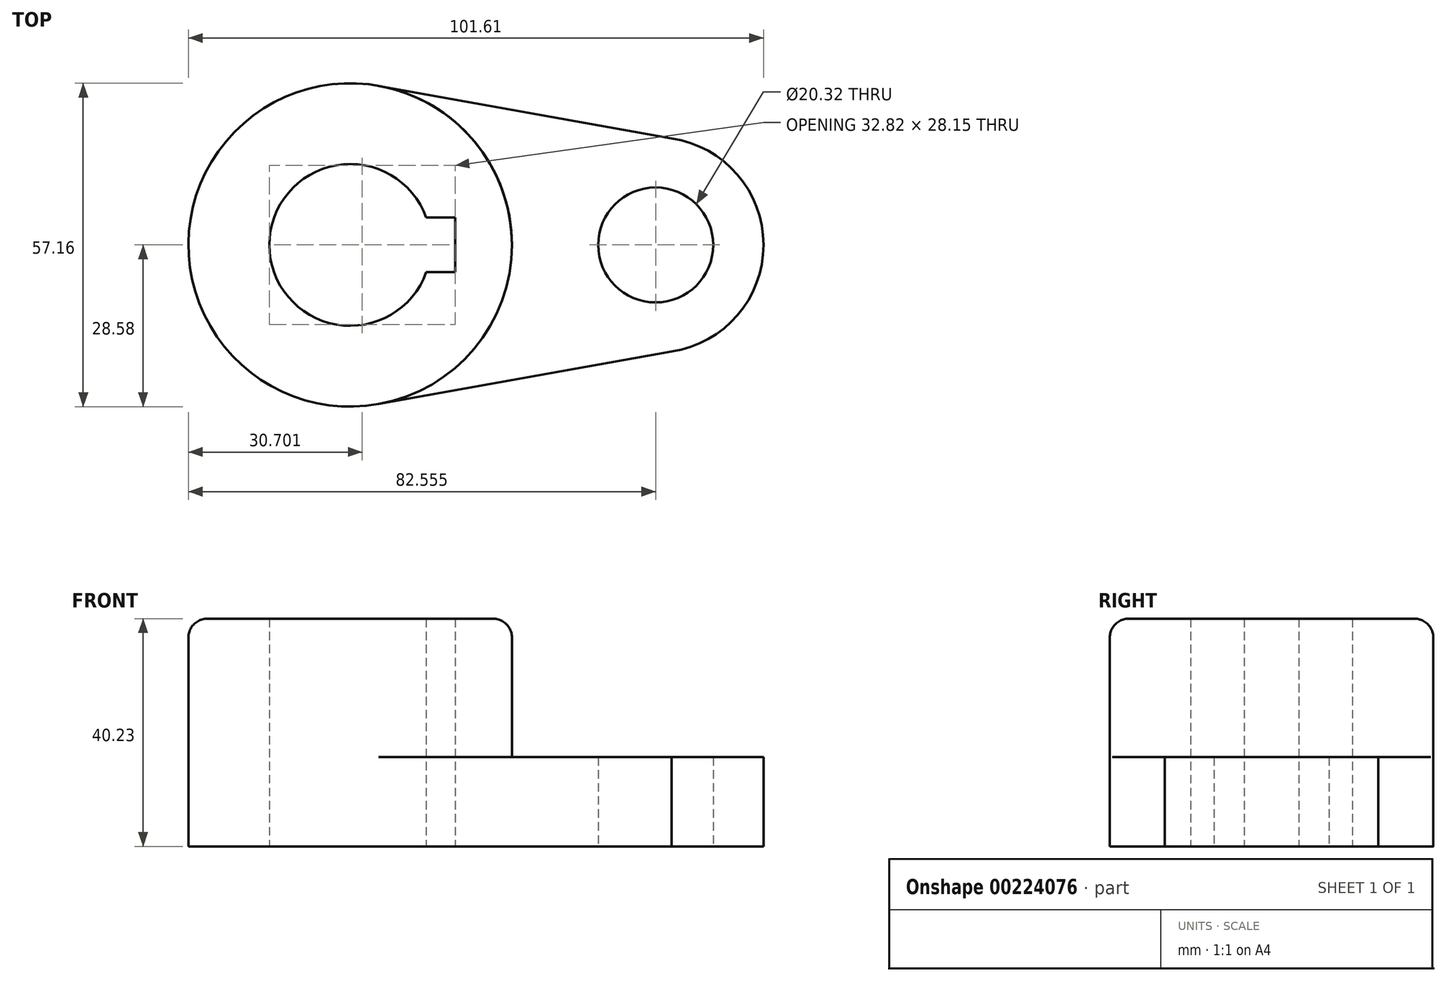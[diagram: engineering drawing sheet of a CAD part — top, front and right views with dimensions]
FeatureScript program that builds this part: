
annotation { "Feature Type Name" : "Feature", "Feature Type Description" : "" }
export const myFeature = defineFeature(function(context is Context, id is Id, definition is map)
    precondition{}
    {
        {
            var Q0;
            Q0=qCreatedBy(makeId("Top.planeOp"),FACE);
            var sketch = newSketch(context, id + "F0", { "sketchPlane" : qUnion([Q0])});
            skLineSegment(sketch, "E0", {"start": v(-44.8, 0) * mm, "end": v(69.93, 0) * mm, "construction": true});
            skCircle(sketch, "E1", {"center": v(0, 0) * mm, "radius": 28.58 * mm});
            skArc(sketch, "E2", {"start": v(13.45, 4.83) * mm, "mid": v(-14.29, 0) * mm, "end": v(13.45, -4.83) * mm});
            skCircle(sketch, "E3", {"center": v(53.98, 0) * mm, "radius": 19.05 * mm});
            skCircle(sketch, "E4", {"center": v(53.98, 0) * mm, "radius": 10.16 * mm});
            skLineSegment(sketch, "E5", {"start": v(-88.6, 4.83) * mm, "end": v(70.66, 4.83) * mm, "construction": true});
            skLineSegment(sketch, "E6", {"start": v(-88.42, -4.83) * mm, "end": v(70.48, -4.83) * mm, "construction": true});
            skLineSegment(sketch, "E7", {"start": v(18.53, -4.83) * mm, "end": v(18.53, 4.83) * mm});
            skLineSegment(sketch, "E8", {"start": v(18.53, 4.83) * mm, "end": v(13.45, 4.83) * mm});
            skLineSegment(sketch, "E9", {"start": v(18.53, -4.83) * mm, "end": v(13.45, -4.83) * mm});
            skLineSegment(sketch, "E10", {"start": v(57.89, 18.64) * mm, "end": v(5.05, 28.13) * mm});
            skLineSegment(sketch, "E11", {"start": v(57.89, -18.64) * mm, "end": v(5.05, -28.13) * mm});
            skSolve(sketch);
        }
        {
            var Q0;
            Q0 = qSketchRegion(id + "F0", true);
            extrude(context, id + "F1", {"entities" : qUnion([Q0]), "depth" : 15.77 * mm});
        }
        {
            var Q0;
            Q0=makeQuery(id+"F0.imprint","IMPRINT",FACE,{"disambiguationData":[TD([[makeQuery(id+"F0.imprint","IMPRINT",EDGE,{"derivedFrom":sQuery(id+"F0.wireOp",EDGE,"E2")}),-1.0]])]});
            extrude(context, id + "F2", {"entities" : qUnion([Q0]), "operationType" : NewBodyOperationType.ADD, "depth" : 40.23 * mm});
        }
        {
            var Q0;
            Q0=makeQuery(id+"F2.opExtrude","CAP_EDGE",EDGE,{"disambiguationData":[OSD([sQuery(id+"F0.wireOp",EDGE,"E1")])],"isStart":false});
            fillet(context, id + "F3", {"entities" : qUnion([Q0]), "radius" : 3.3 * mm, "tangentPropagation" : true, "allowEdgeOverflow" : false});
        }
    });
